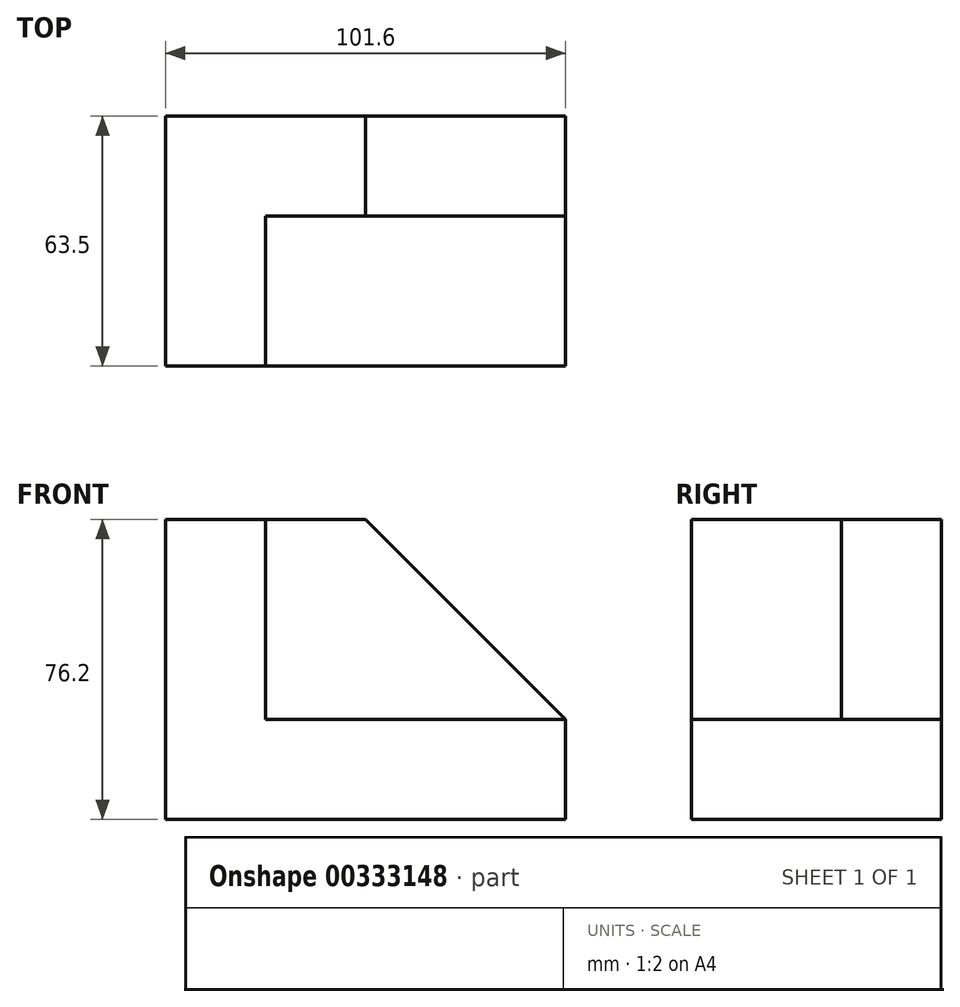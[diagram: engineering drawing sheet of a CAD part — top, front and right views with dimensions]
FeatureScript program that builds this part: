
annotation { "Feature Type Name" : "Feature", "Feature Type Description" : "" }
export const myFeature = defineFeature(function(context is Context, id is Id, definition is map)
    precondition{}
    {
        {
            var Q0;
            Q0=qCreatedBy(makeId("Top.planeOp"),FACE);
            var sketch = newSketch(context, id + "F0", { "sketchPlane" : qUnion([Q0])});
            skLineSegment(sketch, "E0.bottom", {"start": v(-49.74, 34.58) * mm, "end": v(51.86, 34.58) * mm});
            skLineSegment(sketch, "E0.top", {"start": v(-49.74, -28.92) * mm, "end": v(51.86, -28.92) * mm});
            skLineSegment(sketch, "E0.left", {"start": v(-49.74, 34.58) * mm, "end": v(-49.74, -28.92) * mm});
            skLineSegment(sketch, "E0.right", {"start": v(51.86, 34.58) * mm, "end": v(51.86, -28.92) * mm});
            skSolve(sketch);
        }
        {
            var Q0;
            Q0=makeQuery(id+"F0.imprint","IMPRINT",FACE,{"disambiguationData":[TD([[makeQuery(id+"F0.imprint","IMPRINT",EDGE,{"derivedFrom":sQuery(id+"F0.wireOp",EDGE,"E0.bottom")}),-1.0]])]});
            extrude(context, id + "F1", {"entities" : qUnion([Q0]), "depth" : 25.4 * mm});
        }
        {
            var Q0;
            Q0=makeQuery(id+"F1.opExtrude","CAP_FACE",FACE,{"disambiguationData":[OSD([sQuery(id+"F0.wireOp",EDGE,"E0.bottom"),sQuery(id+"F0.wireOp",EDGE,"E0.top"),sQuery(id+"F0.wireOp",EDGE,"E0.left"),sQuery(id+"F0.wireOp",EDGE,"E0.right")])],"isStart":false});
            var sketch = newSketch(context, id + "F2", { "sketchPlane" : qUnion([Q0])});
            skLineSegment(sketch, "E1.bottom", {"start": v(-49.74, -28.92) * mm, "end": v(-24.34, -28.92) * mm});
            skLineSegment(sketch, "E1.top", {"start": v(-49.74, 34.58) * mm, "end": v(-24.34, 34.58) * mm});
            skLineSegment(sketch, "E1.left", {"start": v(-49.74, -28.92) * mm, "end": v(-49.74, 34.58) * mm});
            skLineSegment(sketch, "E1.right", {"start": v(-24.34, -28.92) * mm, "end": v(-24.34, 9.18) * mm});
            skLineSegment(sketch, "E2.bottom", {"start": v(-49.74, 34.58) * mm, "end": v(1.06, 34.58) * mm});
            skLineSegment(sketch, "E2.top", {"start": v(-24.34, 9.18) * mm, "end": v(1.06, 9.18) * mm});
            skLineSegment(sketch, "E2.left", {"start": v(-49.74, 34.58) * mm, "end": v(-49.74, 9.18) * mm});
            skLineSegment(sketch, "E2.right", {"start": v(1.06, 34.58) * mm, "end": v(1.06, 9.18) * mm});
            skSolve(sketch);
        }
        {
            var Q0;
            Q0=makeQuery(id+"F2.imprint","IMPRINT",FACE,{"disambiguationData":[TD([[makeQuery(id+"F2.imprint","IMPRINT",EDGE,{"derivedFrom":sQuery(id+"F2.wireOp",EDGE,"E1.bottom")}),1.0]])]});
            extrude(context, id + "F3", {"entities" : qUnion([Q0]), "operationType" : NewBodyOperationType.ADD, "depth" : 50.8 * mm});
        }
        {
            var Q0;
            Q0=makeQuery(id+"F3.boolean.opBoolean","MERGE",FACE,{"derivedFrom":[makeQuery(id+"F1.opExtrude","SWEPT_FACE",FACE,{"disambiguationData":[OSD([sQuery(id+"F0.wireOp",EDGE,"E0.bottom")])]}),makeQuery(id+"F3.opExtrude","SWEPT_FACE",FACE,{"disambiguationData":[OSD([sQuery(id+"F2.wireOp",EDGE,"E2.bottom")])]})]});
            var sketch = newSketch(context, id + "F4", { "sketchPlane" : qUnion([Q0])});
            skLineSegment(sketch, "E3", {"start": v(-1.06, 76.2) * mm, "end": v(-51.86, 25.4) * mm});
            skSolve(sketch);
        }
        {
            var Q0;
            Q0=makeQuery(id+"F4.imprint","IMPRINT",FACE,{"disambiguationData":[TD([[makeQuery(id+"F4.imprint","IMPRINT",EDGE,{"derivedFrom":sQuery(id+"F4.wireOp",EDGE,"E3")}),1.0]])]});
            extrude(context, id + "F5", {"entities" : qUnion([Q0]), "operationType" : NewBodyOperationType.ADD, "oppositeDirection" : true, "depth" : 25.4 * mm});
        }
    });
